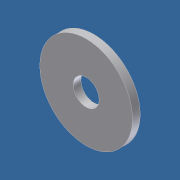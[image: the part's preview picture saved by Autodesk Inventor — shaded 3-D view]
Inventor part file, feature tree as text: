
AUTODESK INVENTOR PART (.ipt)
format: ipt  version: unknown  size: 165,376 bytes
history: native  units: in
note: dims shown in document units (in); Inventor stores cm internally (conversion verified against a paired STEP export)
features: extrude x1, sketch x1
ambient origin geometry x8: Origin, YZ Plane, XZ Plane, XY Plane, X Axis, Y Axis, Z Axis, Center Point
bodies: Solid1 (feature_tree)
feature tree (2):
  extrude  "Extrusion1"  Depth=0.75in
  sketch  "Sketch1"  dims[d0=0.21in d1=0.75in d2=0.0625in d3=0.0in]
